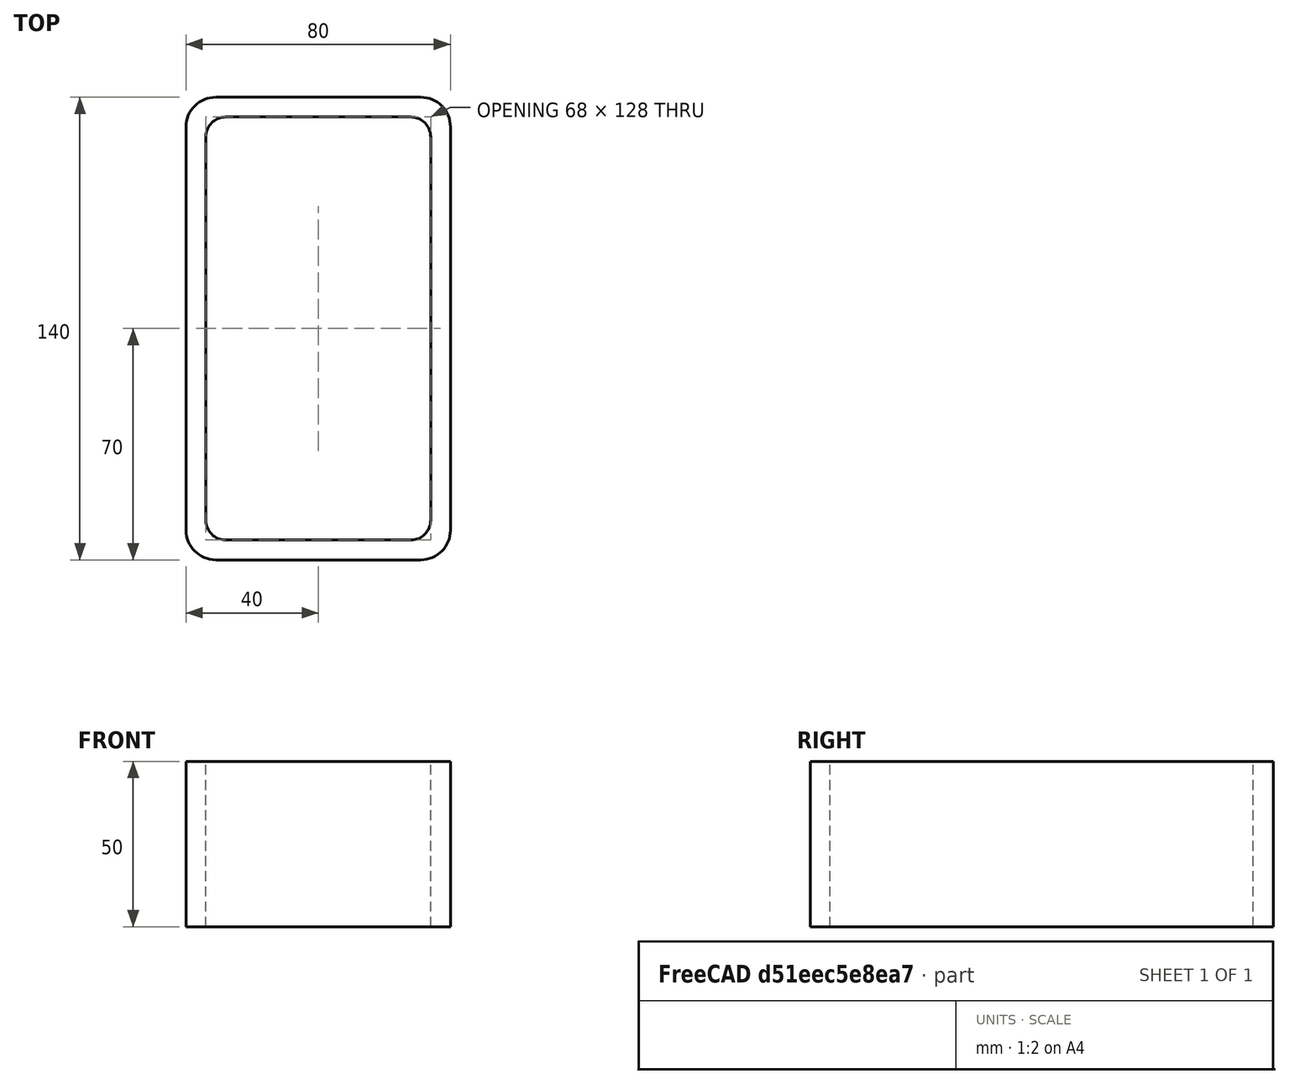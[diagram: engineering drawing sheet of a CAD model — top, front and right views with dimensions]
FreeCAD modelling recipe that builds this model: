
FCSTD DOCUMENT  (FreeCAD 0.15R4671 (Git))
Label: Rectangular hollow section 140x80x6 EN10219 S235JRH
License: All rights reserved
LicenseURL: http://en.wikipedia.org/wiki/All_rights_reserved
objects: Sketcher::SketchObject×1, Part::Extrusion×1
note: 2 computed .brp shape members not serialized (recipe doc carries the construction recipe); baked Part::Feature solids carry a one-line shape summary decoded from their .brp

FEATURE [Sketcher::SketchObject] Sketch
  sketch-geometry (16):
    g0: LineSegment StartX=-28 StartY=64 StartZ=0 EndX=28 EndY=64 EndZ=0
    g1: LineSegment StartX=34 StartY=58 StartZ=0 EndX=34 EndY=-58 EndZ=0
    g2: LineSegment StartX=28 StartY=-64 StartZ=0 EndX=-28 EndY=-64 EndZ=0
    g3: LineSegment StartX=-34 StartY=-58 StartZ=0 EndX=-34 EndY=58 EndZ=0
    g4: LineSegment StartX=-31 StartY=70 StartZ=0 EndX=31 EndY=70 EndZ=0
    g5: LineSegment StartX=40 StartY=61 StartZ=0 EndX=40 EndY=-61 EndZ=0
    g6: LineSegment StartX=31 StartY=-70 StartZ=0 EndX=-31 EndY=-70 EndZ=0
    g7: LineSegment StartX=-40 StartY=-61 StartZ=0 EndX=-40 EndY=61 EndZ=0
    g8: ArcOfCircle CenterX=-28 CenterY=58 CenterZ=0 NormalX=0 NormalY=0 NormalZ=1 Radius=6 StartAngle=1.5708 EndAngle=3.14159
    g9: ArcOfCircle CenterX=28 CenterY=58 CenterZ=0 NormalX=0 NormalY=0 NormalZ=1 Radius=6 StartAngle=0 EndAngle=1.5708
    g10: ArcOfCircle CenterX=28 CenterY=-58 CenterZ=0 NormalX=0 NormalY=0 NormalZ=1 Radius=6 StartAngle=4.71239 EndAngle=6.28319
    g11: ArcOfCircle CenterX=-28 CenterY=-58 CenterZ=0 NormalX=0 NormalY=0 NormalZ=1 Radius=6 StartAngle=3.14159 EndAngle=4.71239
    g12: ArcOfCircle CenterX=31 CenterY=61 CenterZ=0 NormalX=0 NormalY=0 NormalZ=1 Radius=9 StartAngle=0 EndAngle=1.5708
    g13: ArcOfCircle CenterX=31 CenterY=-61 CenterZ=0 NormalX=0 NormalY=0 NormalZ=1 Radius=9 StartAngle=4.71239 EndAngle=6.28319
    g14: ArcOfCircle CenterX=-31 CenterY=-61 CenterZ=0 NormalX=0 NormalY=0 NormalZ=1 Radius=9 StartAngle=3.14159 EndAngle=4.71239
    g15: ArcOfCircle CenterX=-31 CenterY=61 CenterZ=0 NormalX=0 NormalY=0 NormalZ=1 Radius=9 StartAngle=1.5708 EndAngle=3.14159
  constraints (36):
    c: Horizontal(g2)
    c: Vertical(g3)
    c: Horizontal(g6)
    c: Vertical(g7)
    c: Tangent(g3,g8) = 1.5708
    c: Tangent(g0,g8) = 1.5708
    c: Tangent(g0,g9) = 1.5708
    c: Tangent(g1,g9) = 1.5708
    c: Tangent(g1,g10) = 1.5708
    c: Tangent(g2,g10) = 1.5708
    c: Tangent(g2,g11) = 1.5708
    c: Tangent(g3,g11) = 1.5708
    c: Tangent(g4,g12) = 1.5708
    c: Tangent(g5,g12) = 1.5708
    c: Tangent(g5,g13) = 1.5708
    c: Tangent(g6,g13) = 1.5708
    c: Tangent(g6,g14) = 1.5708
    c: Tangent(g7,g14) = 1.5708
    c: Tangent(g7,g15) = 1.5708
    c: Tangent(g4,g15) = 1.5708
    c: Equal(g9,g8)
    c: Equal(g9,g11)
    c: Equal(g9,g10)
    c: Equal(g12,g15)
    c: Equal(g12,g14)
    c: Equal(g12,g13)
    c: Symmetric(g4,g6,g-1)
    c: Symmetric(g7,g5,g-2)
    c: DistanceY(g4,g6) = -140
    c: DistanceX(g7,g5) = 80
    c: Symmetric(g3,g1,g-2)
    c: Symmetric(g0,g2,g-1)
    c: DistanceY(g0,g4) = 6
    c: DistanceX(g5,g1) = -6
    c: Radius(g9) = 6
    c: Radius(g12) = 9
FEATURE [Part::Extrusion] Extrude  label="Rectangular hollow section 140x80x6 EN10219 S235JRH"
  Base = -> Sketch
  Dir = (0,0,50)
  Solid = true
